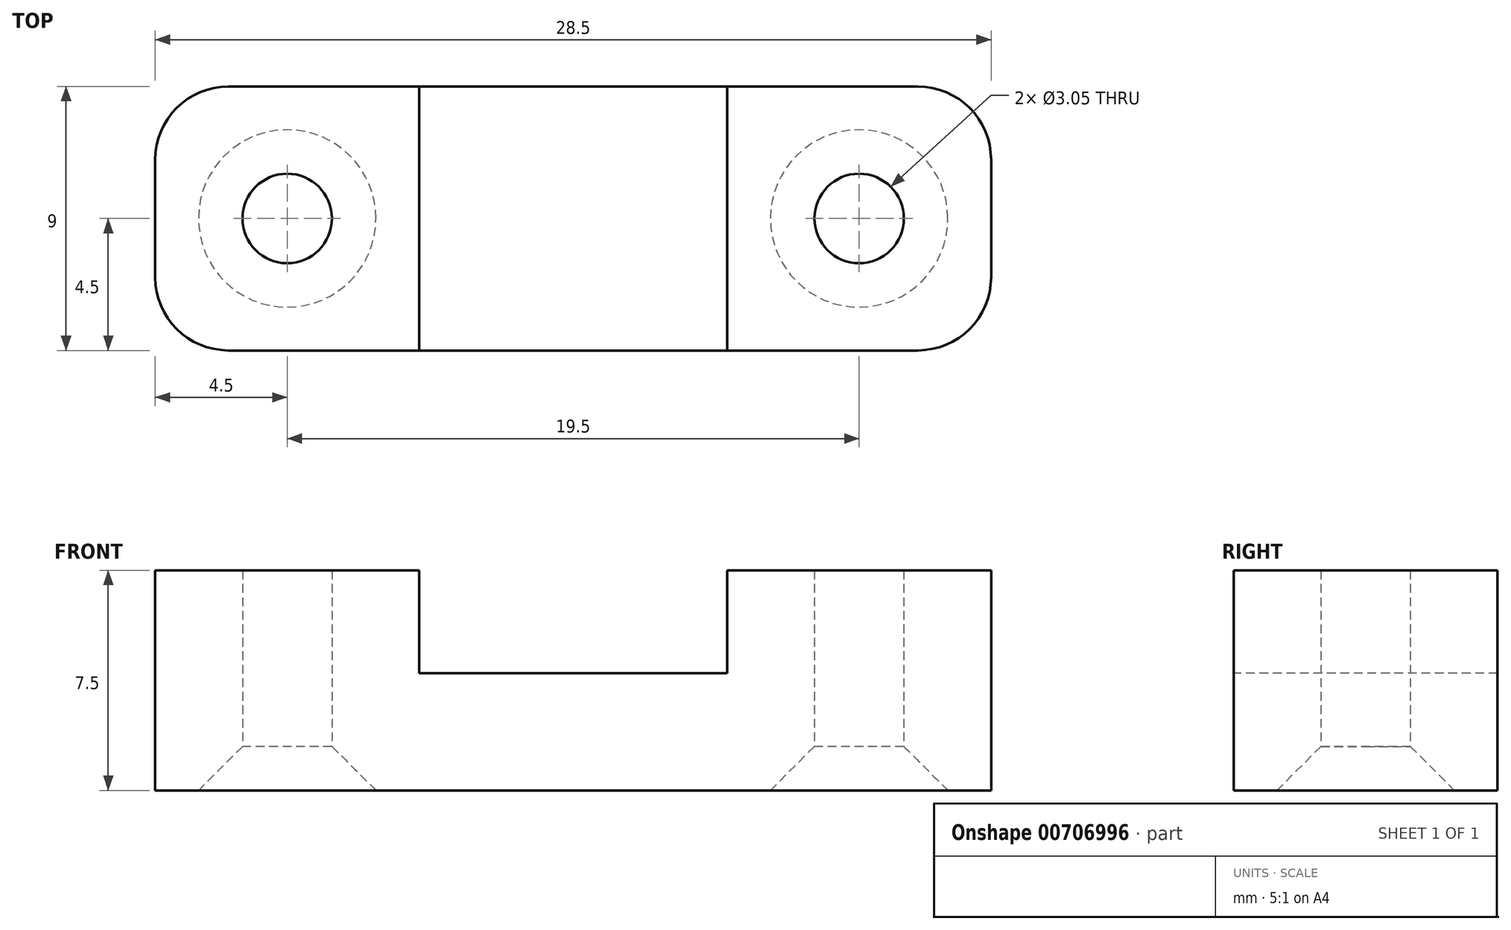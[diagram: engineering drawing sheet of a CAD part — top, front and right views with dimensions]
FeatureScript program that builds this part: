
annotation { "Feature Type Name" : "Feature", "Feature Type Description" : "" }
export const myFeature = defineFeature(function(context is Context, id is Id, definition is map)
    precondition{}
    {
        {
            var Q0;
            Q0=qCreatedBy(makeId("Top.planeOp"),FACE);
            var sketch = newSketch(context, id + "F0", { "sketchPlane" : qUnion([Q0])});
            skLineSegment(sketch, "E0.bottom", {"start": v(14.25, 4.5) * mm, "end": v(-14.25, 4.5) * mm});
            skLineSegment(sketch, "E0.top", {"start": v(14.25, -4.5) * mm, "end": v(-14.25, -4.5) * mm});
            skLineSegment(sketch, "E0.left", {"start": v(14.25, 4.5) * mm, "end": v(14.25, -4.5) * mm});
            skLineSegment(sketch, "E0.right", {"start": v(-14.25, 4.5) * mm, "end": v(-14.25, -4.5) * mm});
            skPoint(sketch, "E0.middle", {"position": v(0, 0) * mm});
            skCircle(sketch, "E1", {"center": v(-9.75, 0) * mm, "radius": 1.52 * mm});
            skCircle(sketch, "E2", {"center": v(9.75, 0) * mm, "radius": 1.52 * mm});
            skSolve(sketch);
        }
        {
            var Q0;
            Q0 = qSketchRegion(id + "F0", true);
            extrude(context, id + "F1", {"entities" : qUnion([Q0]), "depth" : 7.5 * mm, "offsetDistance" : 25 * mm});
        }
        {
            var Q0;
            Q0=makeQuery(id+"F1.opExtrude","CAP_FACE",FACE,{"disambiguationData":[OSD([sQuery(id+"F0.wireOp",EDGE,"E0.bottom"),sQuery(id+"F0.wireOp",EDGE,"E0.top"),sQuery(id+"F0.wireOp",EDGE,"E0.left"),sQuery(id+"F0.wireOp",EDGE,"E0.right"),sQuery(id+"F0.wireOp",EDGE,"E1"),sQuery(id+"F0.wireOp",EDGE,"E2")])],"isStart":false});
            var sketch = newSketch(context, id + "F2", { "sketchPlane" : qUnion([Q0])});
            skLineSegment(sketch, "E3", {"start": v(-5.25, 4.5) * mm, "end": v(-5.25, -4.5) * mm});
            skLineSegment(sketch, "E4", {"start": v(5.25, 4.5) * mm, "end": v(5.25, -4.5) * mm});
            skSolve(sketch);
        }
        {
            var Q0;
            {var subQ0=sQuery(id+"F2.wireOp",EDGE,"E3");Q0=makeQuery(id+"F2.imprint","IMPRINT",FACE,{"disambiguationData":[TD([[makeQuery(id+"F2.imprint","IMPRINT",EDGE,{"derivedFrom":subQ0}),1.0]])]});}
            extrude(context, id + "F3", {"entities" : qUnion([Q0]), "operationType" : NewBodyOperationType.REMOVE, "oppositeDirection" : true, "depth" : 3.5 * mm, "offsetDistance" : 25 * mm});
        }
        {
            var Q0;
            Q0=makeQuery(id+"F1.opExtrude","SWEPT_EDGE",EDGE,{"disambiguationData":[OSD([sQuery(id+"F0.wireOp",EDGE,"E0.top"),sQuery(id+"F0.wireOp",EDGE,"E0.left")])]});
            var Q1;
            Q1=makeQuery(id+"F1.opExtrude","SWEPT_EDGE",EDGE,{"disambiguationData":[OSD([sQuery(id+"F0.wireOp",EDGE,"E0.bottom"),sQuery(id+"F0.wireOp",EDGE,"E0.left")])]});
            var Q2;
            Q2=makeQuery(id+"F1.opExtrude","SWEPT_EDGE",EDGE,{"disambiguationData":[OSD([sQuery(id+"F0.wireOp",EDGE,"E0.top"),sQuery(id+"F0.wireOp",EDGE,"E0.right")])]});
            var Q3;
            Q3=makeQuery(id+"F1.opExtrude","SWEPT_EDGE",EDGE,{"disambiguationData":[OSD([sQuery(id+"F0.wireOp",EDGE,"E0.bottom"),sQuery(id+"F0.wireOp",EDGE,"E0.right")])]});
            fillet(context, id + "F4", {"entities" : qUnion([Q0, Q1, Q2, Q3]), "radius" : 2.5 * mm, "tangentPropagation" : true, "allowEdgeOverflow" : false});
        }
        {
            var Q0;
            Q0=makeQuery(id+"F1.opExtrude","CAP_EDGE",EDGE,{"disambiguationData":[OSD([sQuery(id+"F0.wireOp",EDGE,"E1")])],"isStart":true});
            var Q1;
            Q1=makeQuery(id+"F1.opExtrude","CAP_EDGE",EDGE,{"disambiguationData":[OSD([sQuery(id+"F0.wireOp",EDGE,"E2")])],"isStart":true});
            chamfer(context, id + "F5", {"entities" : qUnion([Q0, Q1]), "chamferType" : ChamferType.TWO_OFFSETS, "width1" : 1.5 * mm, "oppositeDirection" : false, "width2" : 1.5 * mm, "tangentPropagation" : true});
        }
    });
